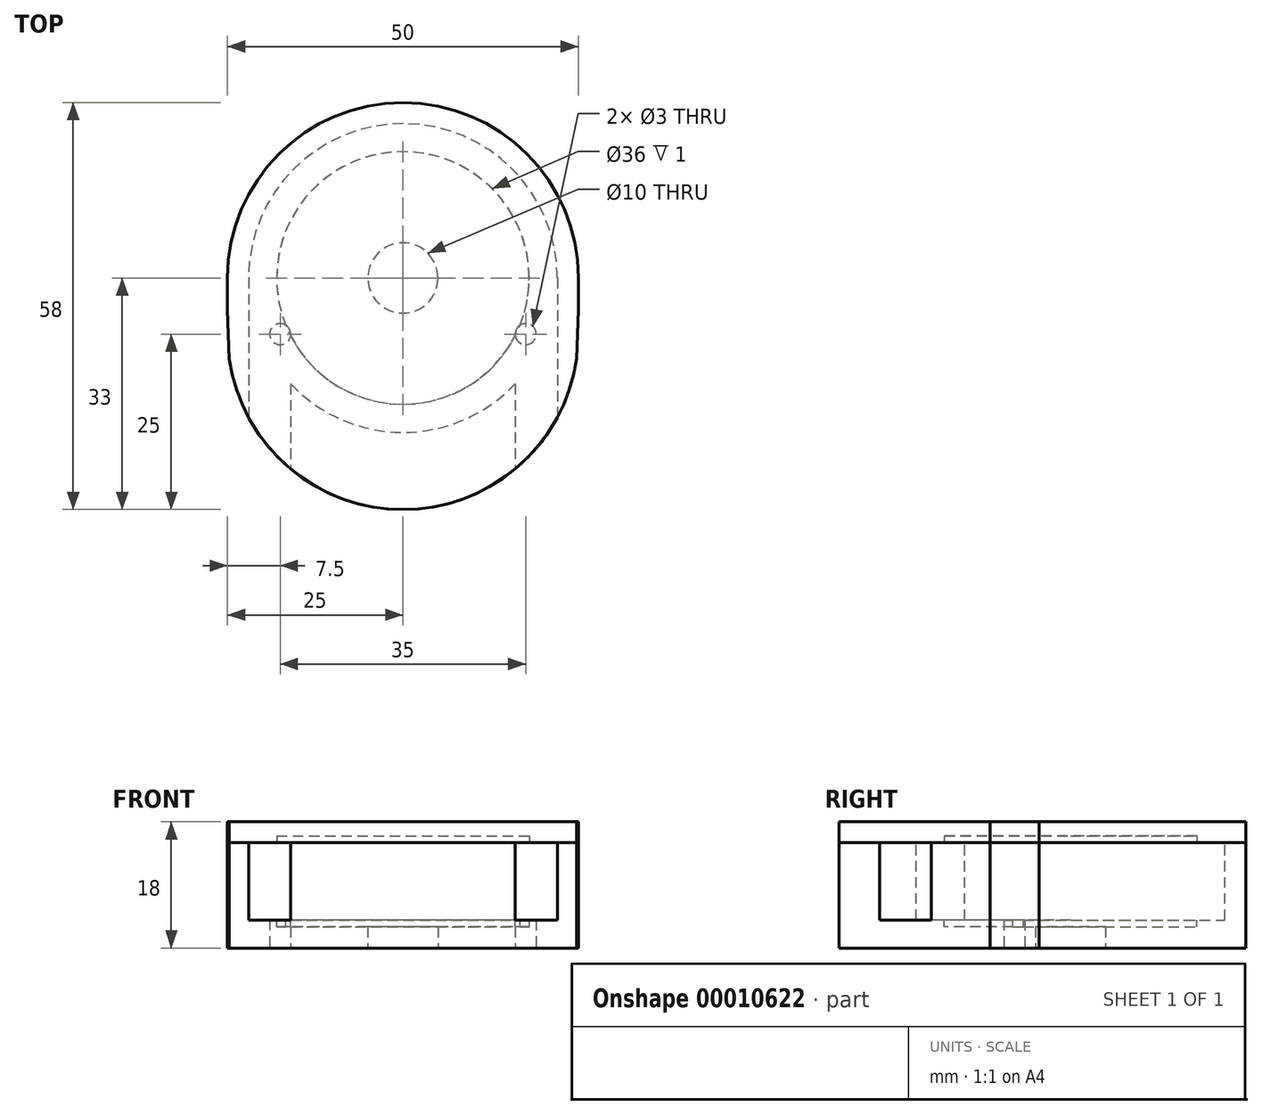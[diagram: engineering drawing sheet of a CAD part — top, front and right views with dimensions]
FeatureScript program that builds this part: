
annotation { "Feature Type Name" : "Feature", "Feature Type Description" : "" }
export const myFeature = defineFeature(function(context is Context, id is Id, definition is map)
    precondition{}
    {
        {
            var Q0;
            Q0=qCreatedBy(makeId("Top.planeOp"),FACE);
            var sketch = newSketch(context, id + "F0", { "sketchPlane" : qUnion([Q0])});
            skArc(sketch, "E0", {"start": v(-24.75, -3.5) * mm, "mid": v(0, -25) * mm, "end": v(24.75, -3.5) * mm});
            skLineSegment(sketch, "E1.rect.bottom", {"start": v(25, 3.5) * mm, "end": v(17.5, 3.5) * mm, "construction": true});
            skLineSegment(sketch, "E1.rect.top", {"start": v(17.5, -3.5) * mm, "end": v(-17.5, -3.5) * mm, "construction": true});
            skLineSegment(sketch, "E1.rect.left", {"start": v(17.5, 3.5) * mm, "end": v(17.5, -3.5) * mm, "construction": true});
            skArc(sketch, "E2", {"start": v(-17.5, 3.5) * mm, "mid": v(-21, 0) * mm, "end": v(-17.5, -3.5) * mm, "construction": true});
            skArc(sketch, "E3", {"start": v(17.5, -3.5) * mm, "mid": v(21, 0) * mm, "end": v(17.5, 3.5) * mm, "construction": true});
            skCircle(sketch, "E4", {"center": v(0, 8) * mm, "radius": 5 * mm});
            skArc(sketch, "E5", {"start": v(25, 8) * mm, "mid": v(0, 33) * mm, "end": v(-25, 8) * mm});
            skLineSegment(sketch, "E6", {"start": v(-25, 8) * mm, "end": v(-25, 3.5) * mm});
            skLineSegment(sketch, "E7", {"start": v(25, 8) * mm, "end": v(25, 3.5) * mm});
            skPoint(sketch, "E8.orphan", {"position": v(-25, 0) * mm});
            skLineSegment(sketch, "E9.trimOffspring", {"start": v(-17.5, 3.5) * mm, "end": v(-25, 3.5) * mm, "construction": true});
            skPoint(sketch, "E10.orphan", {"position": v(25, 0) * mm});
            skCircle(sketch, "E11", {"center": v(-17.5, 0) * mm, "radius": 1.5 * mm});
            skCircle(sketch, "E12", {"center": v(17.5, 0) * mm, "radius": 1.5 * mm});
            skLineSegment(sketch, "E13", {"start": v(-25, 3.5) * mm, "end": v(-24.75, -3.5) * mm});
            skLineSegment(sketch, "E14", {"start": v(25, 3.5) * mm, "end": v(24.75, -3.5) * mm});
            skSolve(sketch);
        }
        {
            var Q0;
            Q0=qSketchRegion(id+"F0",true);
            extrude(context, id + "F1", {"entities" : qUnion([Q0]), "depth" : 15 * mm});
        }
        {
            var Q0;
            Q0=makeQuery(id+"F1.opExtrude","CAP_FACE",FACE,{"disambiguationData":[OSD([sQuery(id+"F0.wireOp",EDGE,"E0"),sQuery(id+"F0.wireOp",EDGE,"E1.rect.bottom"),sQuery(id+"F0.wireOp",EDGE,"E1.rect.top"),sQuery(id+"F0.wireOp",EDGE,"E2"),sQuery(id+"F0.wireOp",EDGE,"E3"),sQuery(id+"F0.wireOp",EDGE,"E4"),sQuery(id+"F0.wireOp",EDGE,"E5"),sQuery(id+"F0.wireOp",EDGE,"E6"),sQuery(id+"F0.wireOp",EDGE,"E7"),sQuery(id+"F0.wireOp",EDGE,"E9.trimOffspring"),sQuery(id+"F0.wireOp",EDGE,"E11"),sQuery(id+"F0.wireOp",EDGE,"E12")])],"isStart":false});
            var sketch = newSketch(context, id + "F2", { "sketchPlane" : qUnion([Q0])});
            skArc(sketch, "E15", {"start": v(-16, -7.1) * mm, "mid": v(0, -14) * mm, "end": v(16, -7.1) * mm});
            skLineSegment(sketch, "E16.bottom", {"start": v(-22, 8) * mm, "end": v(-16, 8) * mm});
            skLineSegment(sketch, "E16.top", {"start": v(-22, -19.2) * mm, "end": v(-16, -19.2) * mm});
            skLineSegment(sketch, "E16.left", {"start": v(-22, 8) * mm, "end": v(-22, -19.2) * mm});
            skLineSegment(sketch, "E16.right", {"start": v(-16, 8) * mm, "end": v(-16, -19.2) * mm});
            skLineSegment(sketch, "E17.bottom", {"start": v(22, 8) * mm, "end": v(16, 8) * mm});
            skLineSegment(sketch, "E17.top", {"start": v(22, -19.2) * mm, "end": v(16, -19.2) * mm});
            skLineSegment(sketch, "E17.left", {"start": v(22, 8) * mm, "end": v(22, -19.2) * mm});
            skLineSegment(sketch, "E17.right", {"start": v(16, 8) * mm, "end": v(16, -19.2) * mm});
            skArc(sketch, "E18.trimOffspring", {"start": v(22, 8) * mm, "mid": v(0, 30) * mm, "end": v(-22, 8) * mm});
            skSolve(sketch);
        }
        {
            var Q0;
            Q0=qSketchRegion(id+"F2",true);
            extrude(context, id + "F3", {"entities" : qUnion([Q0]), "operationType" : NewBodyOperationType.REMOVE, "oppositeDirection" : true, "depth" : 11 * mm});
        }
        {
            var Q0;
            {var subQ0=sQuery(id+"F0.wireOp",EDGE,"E0");Q0=makeQuery(id+"F3.boolean.opBoolean","SPLIT",FACE,{"disambiguationData":[TD([makeQuery(id+"F3.opExtrude","SWEPT_FACE",FACE,{"disambiguationData":[OSD([sQuery(id+"F2.wireOp",EDGE,"E15")])]})])],"derivedFrom":makeQuery(id+"F1.opExtrude","CAP_FACE",FACE,{"disambiguationData":[OSD([subQ0,sQuery(id+"F0.wireOp",EDGE,"E4"),sQuery(id+"F0.wireOp",EDGE,"E5"),sQuery(id+"F0.wireOp",EDGE,"E6"),sQuery(id+"F0.wireOp",EDGE,"E7"),sQuery(id+"F0.wireOp",EDGE,"E11"),sQuery(id+"F0.wireOp",EDGE,"E12"),sQuery(id+"F0.wireOp",EDGE,"E13"),sQuery(id+"F0.wireOp",EDGE,"E14")])],"isStart":false})});}
            var sketch = newSketch(context, id + "F4", { "sketchPlane" : qUnion([Q0])});
            skArc(sketch, "E19.3", {"start": v(-24.75, -3.5) * mm, "mid": v(-23.75, -7.8) * mm, "end": v(-22, -11.87) * mm});
            skArc(sketch, "E20.0", {"start": v(-22, -11.87) * mm, "mid": v(-19.35, -15.83) * mm, "end": v(-16, -19.2) * mm});
            skArc(sketch, "E21.0", {"start": v(-16, -19.2) * mm, "mid": v(0, -25) * mm, "end": v(16, -19.2) * mm});
            skArc(sketch, "E21.1", {"start": v(16, -19.2) * mm, "mid": v(19.35, -15.83) * mm, "end": v(22, -11.87) * mm});
            skArc(sketch, "E21.2", {"start": v(22, -11.87) * mm, "mid": v(23.75, -7.8) * mm, "end": v(24.75, -3.5) * mm});
            skLineSegment(sketch, "E21.3", {"start": v(25, 3.5) * mm, "end": v(24.75, -3.5) * mm});
            skLineSegment(sketch, "E21.4", {"start": v(25, 8) * mm, "end": v(25, 3.5) * mm});
            skArc(sketch, "E21.5", {"start": v(25, 8) * mm, "mid": v(0, 33) * mm, "end": v(-25, 8) * mm});
            skLineSegment(sketch, "E21.6", {"start": v(-25, 8) * mm, "end": v(-25, 3.5) * mm});
            skLineSegment(sketch, "E21.7", {"start": v(-25, 3.5) * mm, "end": v(-24.75, -3.5) * mm});
            skSolve(sketch);
        }
        {
            var Q0;
            Q0=qSketchRegion(id+"F4",true);
            extrude(context, id + "F5", {"entities" : qUnion([Q0]), "depth" : 3 * mm});
        }
        {
            var Q0;
            Q0=makeQuery(id+"F3.boolean.opBoolean","COPY",FACE,{"derivedFrom":makeQuery(id+"F3.opExtrude","CAP_FACE",FACE,{"disambiguationData":[OSD([sQuery(id+"F2.wireOp",EDGE,"E15"),sQuery(id+"F2.wireOp",EDGE,"E16.top"),sQuery(id+"F2.wireOp",EDGE,"E16.left"),sQuery(id+"F2.wireOp",EDGE,"E16.right"),sQuery(id+"F2.wireOp",EDGE,"E17.top"),sQuery(id+"F2.wireOp",EDGE,"E17.left"),sQuery(id+"F2.wireOp",EDGE,"E17.right"),sQuery(id+"F2.wireOp",EDGE,"E18.trimOffspring")])],"isStart":false})});
            var sketch = newSketch(context, id + "F6", { "sketchPlane" : qUnion([Q0])});
            skCircle(sketch, "E22", {"center": v(0, 8) * mm, "radius": 18 * mm});
            skSolve(sketch);
        }
        {
            var Q0;
            Q0 = qSketchRegion(id + "F6", true);
            extrude(context, id + "F7", {"entities" : qUnion([Q0]), "operationType" : NewBodyOperationType.REMOVE, "oppositeDirection" : true, "depth" : 1 * mm});
        }
        {
            var Q0;
            Q0=makeQuery(id+"F5.opExtrude","CAP_FACE",FACE,{"disambiguationData":[OSD([sQuery(id+"F4.wireOp",EDGE,"E19.3"),sQuery(id+"F4.wireOp",EDGE,"E20.0"),sQuery(id+"F4.wireOp",EDGE,"E21.0"),sQuery(id+"F4.wireOp",EDGE,"E21.1"),sQuery(id+"F4.wireOp",EDGE,"E21.2"),sQuery(id+"F4.wireOp",EDGE,"E21.3"),sQuery(id+"F4.wireOp",EDGE,"E21.4"),sQuery(id+"F4.wireOp",EDGE,"E21.5"),sQuery(id+"F4.wireOp",EDGE,"E21.6"),sQuery(id+"F4.wireOp",EDGE,"E21.7")])],"isStart":true});
            var sketch = newSketch(context, id + "F8", { "sketchPlane" : qUnion([Q0])});
            skCircle(sketch, "E23.0", {"center": v(0, -8) * mm, "radius": 18 * mm});
            skSolve(sketch);
        }
        {
            var Q0;
            Q0 = qSketchRegion(id + "F8", true);
            extrude(context, id + "F9", {"entities" : qUnion([Q0]), "operationType" : NewBodyOperationType.REMOVE, "oppositeDirection" : true, "depth" : 1 * mm});
        }
    });
